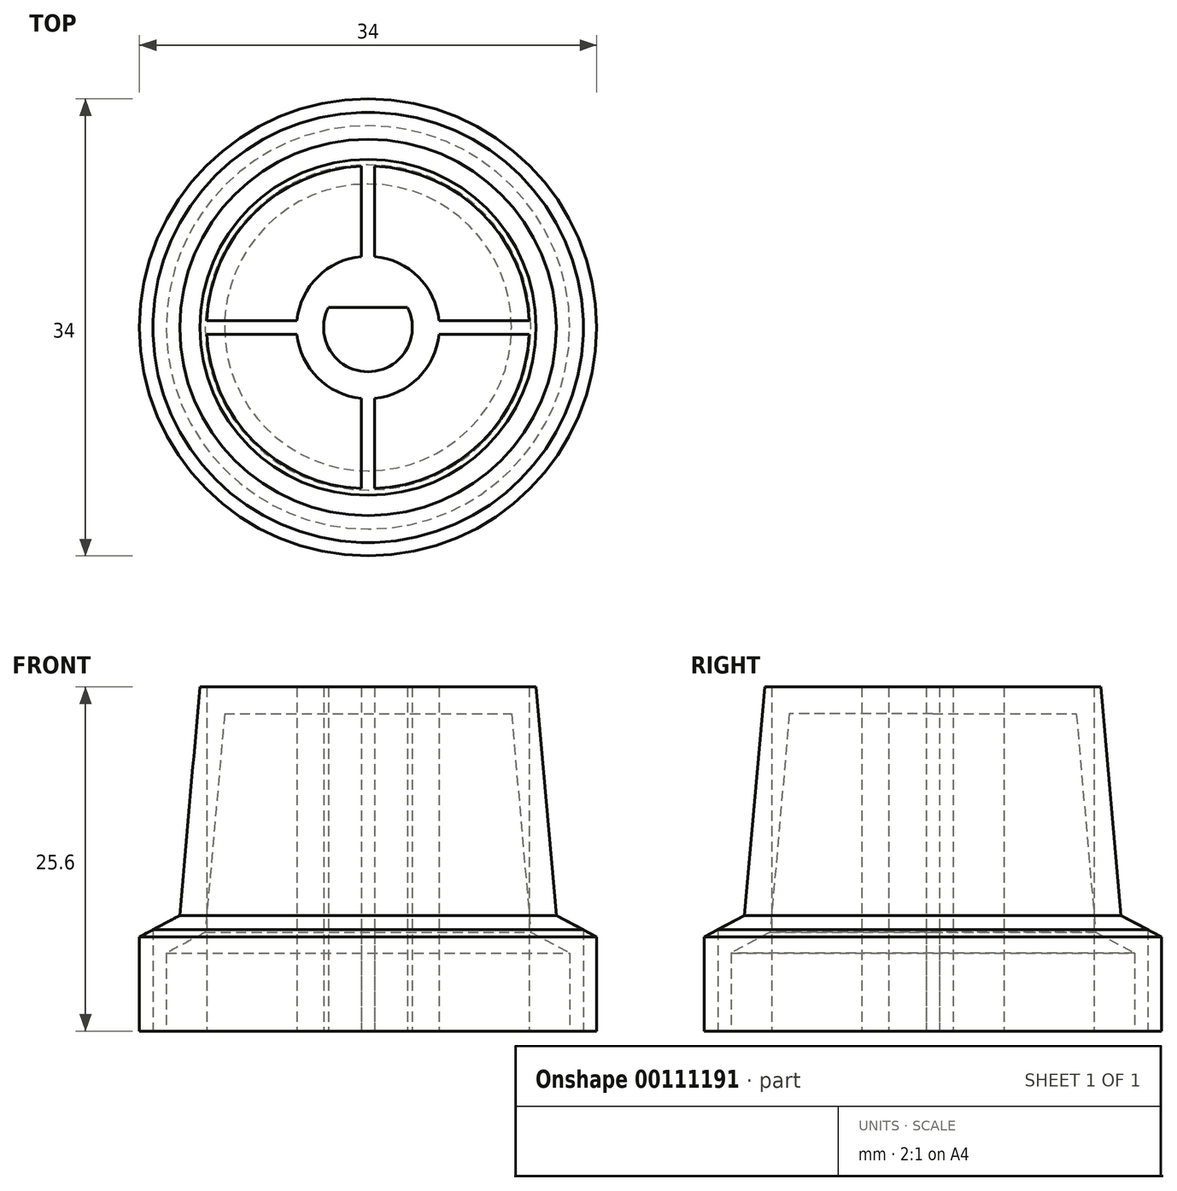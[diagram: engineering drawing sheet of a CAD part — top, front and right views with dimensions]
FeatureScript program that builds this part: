
annotation { "Feature Type Name" : "Feature", "Feature Type Description" : "" }
export const myFeature = defineFeature(function(context is Context, id is Id, definition is map)
    precondition{}
    {
        {
            var Q0;
            Q0=qCreatedBy(makeId("Top.planeOp"),FACE);
            var sketch = newSketch(context, id + "F0", { "sketchPlane" : qUnion([Q0])});
            skArc(sketch, "E0", {"start": v(-2.94, 1.5) * mm, "mid": v(0, -3.3) * mm, "end": v(2.94, 1.5) * mm});
            skLineSegment(sketch, "E1", {"start": v(-2.94, 1.5) * mm, "end": v(2.94, 1.5) * mm});
            skCircle(sketch, "E2", {"center": v(0, 0) * mm, "radius": 5.3 * mm});
            skLineSegment(sketch, "E3", {"start": v(-48.9, 0) * mm, "end": v(49.86, 0) * mm, "construction": true});
            skLineSegment(sketch, "E4.bottom", {"start": v(-16, 0.5) * mm, "end": v(0, 0.5) * mm});
            skLineSegment(sketch, "E4.top", {"start": v(-16, -0.5) * mm, "end": v(0, -0.5) * mm});
            skLineSegment(sketch, "E4.left", {"start": v(-16, 0.5) * mm, "end": v(-16, -0.5) * mm});
            skLineSegment(sketch, "E4.right", {"start": v(0, 0.5) * mm, "end": v(0, -0.5) * mm});
            skLineSegment(sketch, "E5.3.1", {"start": v(0, 15.5) * mm, "end": v(-1, 15.5) * mm});
            skLineSegment(sketch, "E6.1.0", {"start": v(-0.5, -16) * mm, "end": v(-0.5, 0) * mm});
            skLineSegment(sketch, "E6.1.1", {"start": v(0.5, -16) * mm, "end": v(0.5, 0) * mm});
            skLineSegment(sketch, "E6.1.2", {"start": v(-0.5, -16) * mm, "end": v(0.5, -16) * mm});
            skLineSegment(sketch, "E6.1.3", {"start": v(-0.5, 0) * mm, "end": v(0.5, 0) * mm});
            skLineSegment(sketch, "E6.2.0", {"start": v(16, -0.5) * mm, "end": v(0, -0.5) * mm});
            skLineSegment(sketch, "E6.2.1", {"start": v(16, 0.5) * mm, "end": v(0, 0.5) * mm});
            skLineSegment(sketch, "E6.2.2", {"start": v(16, -0.5) * mm, "end": v(16, 0.5) * mm});
            skLineSegment(sketch, "E6.2.3", {"start": v(0, -0.5) * mm, "end": v(0, 0.5) * mm});
            skLineSegment(sketch, "E6.3.0", {"start": v(0.5, 16) * mm, "end": v(0.5, 0) * mm});
            skLineSegment(sketch, "E6.3.1", {"start": v(-0.5, 16) * mm, "end": v(-0.5, 0) * mm});
            skLineSegment(sketch, "E6.3.2", {"start": v(0.5, 16) * mm, "end": v(-0.5, 16) * mm});
            skLineSegment(sketch, "E6.3.3", {"start": v(0.5, 0) * mm, "end": v(-0.5, 0) * mm});
            skCircle(sketch, "E7", {"center": v(0, 0) * mm, "radius": 12 * mm});
            skCircle(sketch, "E8", {"center": v(0, 0) * mm, "radius": 16 * mm});
            skSolve(sketch);
        }
        {
            var Q0;
            Q0=qCreatedBy(makeId("Front.planeOp"),FACE);
            var sketch = newSketch(context, id + "F1", { "sketchPlane" : qUnion([Q0])});
            skLineSegment(sketch, "E9", {"start": v(-41.22, 0) * mm, "end": v(42.4, 0) * mm, "construction": true});
            skLineSegment(sketch, "E10", {"start": v(42.4, 0) * mm, "end": v(0, 0) * mm, "construction": true});
            skLineSegment(sketch, "E11", {"start": v(0, 0) * mm, "end": v(0, 52.33) * mm, "construction": true});
            skLineSegment(sketch, "E12", {"start": v(0, 0) * mm, "end": v(17, 0) * mm});
            skLineSegment(sketch, "E13", {"start": v(14, 8.6) * mm, "end": v(12.5, 25.6) * mm});
            skLineSegment(sketch, "E14", {"start": v(12.5, 25.6) * mm, "end": v(0, 25.6) * mm});
            skLineSegment(sketch, "E15", {"start": v(0, 25.6) * mm, "end": v(0, 0) * mm});
            skLineSegment(sketch, "E16", {"start": v(17, 0) * mm, "end": v(17, 7) * mm});
            skLineSegment(sketch, "E17", {"start": v(17, 7) * mm, "end": v(14, 8.6) * mm});
            skSolve(sketch);
        }
        {
            var Q0;
            Q0=makeQuery(id+"F1.imprint","IMPRINT",FACE,{"disambiguationData":[TD([[makeQuery(id+"F1.imprint","IMPRINT",EDGE,{"derivedFrom":sQuery(id+"F1.wireOp",EDGE,"E12")}),1.0]])]});
            var Q1;
            Q1=sQuery(id+"F1.wireOp",EDGE,"E11");
            revolve(context, id + "F2", {"entities" : qUnion([Q0]), "axis" : qUnion([Q1]), "revolveType" : RevolveType.FULL});
        }
        {
            var Q0;
            {var subQ5=sQuery(id+"F0.wireOp",EDGE,"E4.left");Q0=makeQuery(id+"F0.imprint","IMPRINT",FACE,{"disambiguationData":[TD([[makeQuery(id+"F0.imprint","IMPRINT",EDGE,{"derivedFrom":subQ5}),1.0]])]});}
            var Q1;
            {var subQ0=sQuery(id+"F0.wireOp",EDGE,"E4.top");var subQ1=sQuery(id+"F0.wireOp",EDGE,"E0");var subQ2=makeQuery(id+"F0.imprint","INTERSECT",VERTEX,{"derivedFrom":[subQ1,subQ0]});Q1=makeQuery(id+"F0.imprint","IMPRINT",FACE,{"disambiguationData":[TD([[makeQuery(id+"F0.imprint","IMPRINT",EDGE,{"disambiguationData":[TD([[subQ2,-1.0]])],"derivedFrom":subQ1}),-1.0]])]});}
            var Q2;
            {var subQ5=sQuery(id+"F0.wireOp",EDGE,"E0");var subQ7=sQuery(id+"F0.wireOp",EDGE,"E1");var subQ8=makeQuery(id+"F0.imprint","INTERSECT",VERTEX,{"disambiguationData":[OD(0.0)],"derivedFrom":[subQ5,subQ7]});Q2=makeQuery(id+"F0.imprint","IMPRINT",FACE,{"disambiguationData":[TD([[makeQuery(id+"F0.imprint","IMPRINT",EDGE,{"disambiguationData":[TD([[subQ8,-1.0]])],"derivedFrom":subQ5}),-1.0]])]});}
            var Q3;
            {var subQ0=sQuery(id+"F0.wireOp",EDGE,"E4.bottom");var subQ1=sQuery(id+"F0.wireOp",EDGE,"E0");var subQ2=makeQuery(id+"F0.imprint","INTERSECT",VERTEX,{"derivedFrom":[subQ1,subQ0]});Q3=makeQuery(id+"F0.imprint","IMPRINT",FACE,{"disambiguationData":[TD([[makeQuery(id+"F0.imprint","IMPRINT",EDGE,{"disambiguationData":[TD([[subQ2,-1.0]])],"derivedFrom":subQ1}),-1.0]])]});}
            var Q4;
            {var subQ5=sQuery(id+"F0.wireOp",EDGE,"E6.1.2");Q4=makeQuery(id+"F0.imprint","IMPRINT",FACE,{"disambiguationData":[TD([[makeQuery(id+"F0.imprint","IMPRINT",EDGE,{"derivedFrom":subQ5}),1.0]])]});}
            var Q5;
            {var subQ0=sQuery(id+"F0.wireOp",EDGE,"E6.1.0");var subQ1=sQuery(id+"F0.wireOp",EDGE,"E0");var subQ2=makeQuery(id+"F0.imprint","INTERSECT",VERTEX,{"derivedFrom":[subQ1,subQ0]});Q5=makeQuery(id+"F0.imprint","IMPRINT",FACE,{"disambiguationData":[TD([[makeQuery(id+"F0.imprint","IMPRINT",EDGE,{"disambiguationData":[TD([[subQ2,-1.0]])],"derivedFrom":subQ1}),-1.0]])]});}
            var Q6;
            {var subQ0=sQuery(id+"F0.wireOp",EDGE,"E6.1.1");var subQ1=sQuery(id+"F0.wireOp",EDGE,"E0");var subQ2=makeQuery(id+"F0.imprint","INTERSECT",VERTEX,{"derivedFrom":[subQ1,subQ0]});Q6=makeQuery(id+"F0.imprint","IMPRINT",FACE,{"disambiguationData":[TD([[makeQuery(id+"F0.imprint","IMPRINT",EDGE,{"disambiguationData":[TD([[subQ2,-1.0]])],"derivedFrom":subQ1}),-1.0]])]});}
            var Q7;
            {var subQ0=sQuery(id+"F0.wireOp",EDGE,"E6.2.0");var subQ1=sQuery(id+"F0.wireOp",EDGE,"E0");var subQ2=makeQuery(id+"F0.imprint","INTERSECT",VERTEX,{"derivedFrom":[subQ1,subQ0]});Q7=makeQuery(id+"F0.imprint","IMPRINT",FACE,{"disambiguationData":[TD([[makeQuery(id+"F0.imprint","IMPRINT",EDGE,{"disambiguationData":[TD([[subQ2,-1.0]])],"derivedFrom":subQ1}),-1.0]])]});}
            var Q8;
            {var subQ5=sQuery(id+"F0.wireOp",EDGE,"E6.2.2");Q8=makeQuery(id+"F0.imprint","IMPRINT",FACE,{"disambiguationData":[TD([[makeQuery(id+"F0.imprint","IMPRINT",EDGE,{"derivedFrom":subQ5}),1.0]])]});}
            var Q9;
            {var subQ3=sQuery(id+"F0.wireOp",EDGE,"E0");var subQ7=sQuery(id+"F0.wireOp",EDGE,"E1");var subQ8=makeQuery(id+"F0.imprint","INTERSECT",VERTEX,{"disambiguationData":[OD(1.0)],"derivedFrom":[subQ3,subQ7]});Q9=makeQuery(id+"F0.imprint","IMPRINT",FACE,{"disambiguationData":[TD([[makeQuery(id+"F0.imprint","IMPRINT",EDGE,{"disambiguationData":[TD([[subQ8,1.0]])],"derivedFrom":subQ3}),-1.0]])]});}
            var Q10;
            {var subQ0=sQuery(id+"F0.wireOp",EDGE,"E6.3.1");var subQ1=sQuery(id+"F0.wireOp",EDGE,"E1");var subQ2=makeQuery(id+"F0.imprint","INTERSECT",VERTEX,{"derivedFrom":[subQ1,subQ0]});Q10=makeQuery(id+"F0.imprint","IMPRINT",FACE,{"disambiguationData":[TD([[makeQuery(id+"F0.imprint","IMPRINT",EDGE,{"disambiguationData":[TD([[subQ2,-1.0]])],"derivedFrom":subQ1}),1.0]])]});}
            var Q11;
            {var subQ5=sQuery(id+"F0.wireOp",EDGE,"E6.3.2");Q11=makeQuery(id+"F0.imprint","IMPRINT",FACE,{"disambiguationData":[TD([[makeQuery(id+"F0.imprint","IMPRINT",EDGE,{"derivedFrom":subQ5}),1.0]])]});}
            var Q12;
            {var subQ1=sQuery(id+"F0.wireOp",EDGE,"E4.top");var subQ3=sQuery(id+"F0.wireOp",EDGE,"E7");var subQ4=makeQuery(id+"F0.imprint","INTERSECT",VERTEX,{"derivedFrom":[subQ1,subQ3]});Q12=makeQuery(id+"F0.imprint","IMPRINT",FACE,{"disambiguationData":[TD([[makeQuery(id+"F0.imprint","IMPRINT",EDGE,{"disambiguationData":[TD([[subQ4,-1.0]])],"derivedFrom":subQ3}),-1.0]])]});}
            var Q13;
            {var subQ1=sQuery(id+"F0.wireOp",EDGE,"E6.1.1");var subQ3=sQuery(id+"F0.wireOp",EDGE,"E7");var subQ4=makeQuery(id+"F0.imprint","INTERSECT",VERTEX,{"derivedFrom":[subQ1,subQ3]});Q13=makeQuery(id+"F0.imprint","IMPRINT",FACE,{"disambiguationData":[TD([[makeQuery(id+"F0.imprint","IMPRINT",EDGE,{"disambiguationData":[TD([[subQ4,-1.0]])],"derivedFrom":subQ3}),-1.0]])]});}
            var Q14;
            {var subQ1=sQuery(id+"F0.wireOp",EDGE,"E6.2.1");var subQ3=sQuery(id+"F0.wireOp",EDGE,"E7");var subQ4=makeQuery(id+"F0.imprint","INTERSECT",VERTEX,{"derivedFrom":[subQ1,subQ3]});Q14=makeQuery(id+"F0.imprint","IMPRINT",FACE,{"disambiguationData":[TD([[makeQuery(id+"F0.imprint","IMPRINT",EDGE,{"disambiguationData":[TD([[subQ4,-1.0]])],"derivedFrom":subQ3}),-1.0]])]});}
            var Q15;
            {var subQ0=sQuery(id+"F0.wireOp",EDGE,"E6.3.1");var subQ1=makeQuery(id+"F0.imprint","IMPRINT",VERTEX,{"derivedFrom":subQ0});Q15=makeQuery(id+"F0.imprint","IMPRINT",FACE,{"disambiguationData":[TD([[makeQuery(id+"F0.imprint","IMPRINT",EDGE,{"disambiguationData":[TD([[subQ1,-1.0]])],"derivedFrom":subQ0}),-1.0]])]});}
            var Q16;
            {var subQ0=sQuery(id+"F0.wireOp",EDGE,"E4.bottom");var subQ1=sQuery(id+"F0.wireOp",EDGE,"E2");var subQ2=makeQuery(id+"F0.imprint","INTERSECT",VERTEX,{"derivedFrom":[subQ1,subQ0]});Q16=makeQuery(id+"F0.imprint","IMPRINT",FACE,{"disambiguationData":[TD([[makeQuery(id+"F0.imprint","IMPRINT",EDGE,{"disambiguationData":[TD([[subQ2,-1.0]])],"derivedFrom":subQ1}),-1.0]])]});}
            var Q17;
            {var subQ0=sQuery(id+"F0.wireOp",EDGE,"E6.1.0");var subQ1=sQuery(id+"F0.wireOp",EDGE,"E2");var subQ2=makeQuery(id+"F0.imprint","INTERSECT",VERTEX,{"derivedFrom":[subQ1,subQ0]});Q17=makeQuery(id+"F0.imprint","IMPRINT",FACE,{"disambiguationData":[TD([[makeQuery(id+"F0.imprint","IMPRINT",EDGE,{"disambiguationData":[TD([[subQ2,-1.0]])],"derivedFrom":subQ1}),-1.0]])]});}
            var Q18;
            {var subQ0=sQuery(id+"F0.wireOp",EDGE,"E6.2.1");var subQ1=sQuery(id+"F0.wireOp",EDGE,"E2");var subQ2=makeQuery(id+"F0.imprint","INTERSECT",VERTEX,{"derivedFrom":[subQ1,subQ0]});Q18=makeQuery(id+"F0.imprint","IMPRINT",FACE,{"disambiguationData":[TD([[makeQuery(id+"F0.imprint","IMPRINT",EDGE,{"disambiguationData":[TD([[subQ2,1.0]])],"derivedFrom":subQ1}),-1.0]])]});}
            var Q19;
            {var subQ0=sQuery(id+"F0.wireOp",EDGE,"E6.3.0");var subQ1=sQuery(id+"F0.wireOp",EDGE,"E2");var subQ2=makeQuery(id+"F0.imprint","INTERSECT",VERTEX,{"derivedFrom":[subQ1,subQ0]});Q19=makeQuery(id+"F0.imprint","IMPRINT",FACE,{"disambiguationData":[TD([[makeQuery(id+"F0.imprint","IMPRINT",EDGE,{"disambiguationData":[TD([[subQ2,-1.0]])],"derivedFrom":subQ1}),-1.0]])]});}
            var Q20;
            Q20=makeQuery(id+"F2.opRevolve","SWEPT_FACE",FACE,{"disambiguationData":[OSD([sQuery(id+"F1.wireOp",EDGE,"E14")])]});
            extrude(context, id + "F3", {"entities" : qUnion([Q0, Q1, Q2, Q3, Q4, Q5, Q6, Q7, Q8, Q9, Q10, Q11, Q12, Q13, Q14, Q15, Q16, Q17, Q18, Q19]), "endBound" : BoundingType.UP_TO_SURFACE, "endBoundEntityFace" : qUnion([Q20]), "depth" : 25 * mm});
        }
        {
            var Q0;
            Q0=makeQuery(id+"F3.opExtrude","SWEPT_BODY",BODY,{"disambiguationData":[OSD([sQuery(id+"F0.wireOp",EDGE,"E0"),sQuery(id+"F0.wireOp",EDGE,"E1"),sQuery(id+"F0.wireOp",EDGE,"E2"),sQuery(id+"F0.wireOp",EDGE,"E4.bottom"),sQuery(id+"F0.wireOp",EDGE,"E4.top"),sQuery(id+"F0.wireOp",EDGE,"E4.left"),sQuery(id+"F0.wireOp",EDGE,"E6.1.0"),sQuery(id+"F0.wireOp",EDGE,"E6.1.1"),sQuery(id+"F0.wireOp",EDGE,"E6.1.2"),sQuery(id+"F0.wireOp",EDGE,"E6.2.0"),sQuery(id+"F0.wireOp",EDGE,"E6.2.1"),sQuery(id+"F0.wireOp",EDGE,"E6.2.2"),sQuery(id+"F0.wireOp",EDGE,"E6.3.0"),sQuery(id+"F0.wireOp",EDGE,"E6.3.1"),sQuery(id+"F0.wireOp",EDGE,"E6.3.2")])]});
            var Q1;
            Q1=makeQuery(id+"F2.opRevolve","SWEPT_BODY",BODY,{"disambiguationData":[OSD([sQuery(id+"F1.wireOp",EDGE,"E12"),sQuery(id+"F1.wireOp",EDGE,"E13"),sQuery(id+"F1.wireOp",EDGE,"E14"),sQuery(id+"F1.wireOp",EDGE,"E15"),sQuery(id+"F1.wireOp",EDGE,"E16"),sQuery(id+"F1.wireOp",EDGE,"E17")])]});
            booleanBodies(context, id + "F4", {"operationType" : BooleanOperationType.INTERSECTION, "tools" : qUnion([Q0, Q1]), "keepTools" : true});
        }
        {
            var Q0;
            Q0=makeQuery(id+"F3.opExtrude","SWEPT_BODY",BODY,{"disambiguationData":[OSD([sQuery(id+"F0.wireOp",EDGE,"E0"),sQuery(id+"F0.wireOp",EDGE,"E1"),sQuery(id+"F0.wireOp",EDGE,"E2"),sQuery(id+"F0.wireOp",EDGE,"E4.bottom"),sQuery(id+"F0.wireOp",EDGE,"E4.top"),sQuery(id+"F0.wireOp",EDGE,"E4.left"),sQuery(id+"F0.wireOp",EDGE,"E6.1.0"),sQuery(id+"F0.wireOp",EDGE,"E6.1.1"),sQuery(id+"F0.wireOp",EDGE,"E6.1.2"),sQuery(id+"F0.wireOp",EDGE,"E6.2.0"),sQuery(id+"F0.wireOp",EDGE,"E6.2.1"),sQuery(id+"F0.wireOp",EDGE,"E6.2.2"),sQuery(id+"F0.wireOp",EDGE,"E6.3.0"),sQuery(id+"F0.wireOp",EDGE,"E6.3.1"),sQuery(id+"F0.wireOp",EDGE,"E6.3.2")])]});
            deleteBodies(context, id + "F5", {"entities" : qUnion([Q0])});
        }
        {
            var Q0;
            Q0=makeQuery(id+"F2.opRevolve","SWEPT_FACE",FACE,{"disambiguationData":[OSD([sQuery(id+"F1.wireOp",EDGE,"E12")])]});
            shell(context, id + "F6", {"entities" : qUnion([Q0]), "thickness" : 2 * mm});
        }
    });
